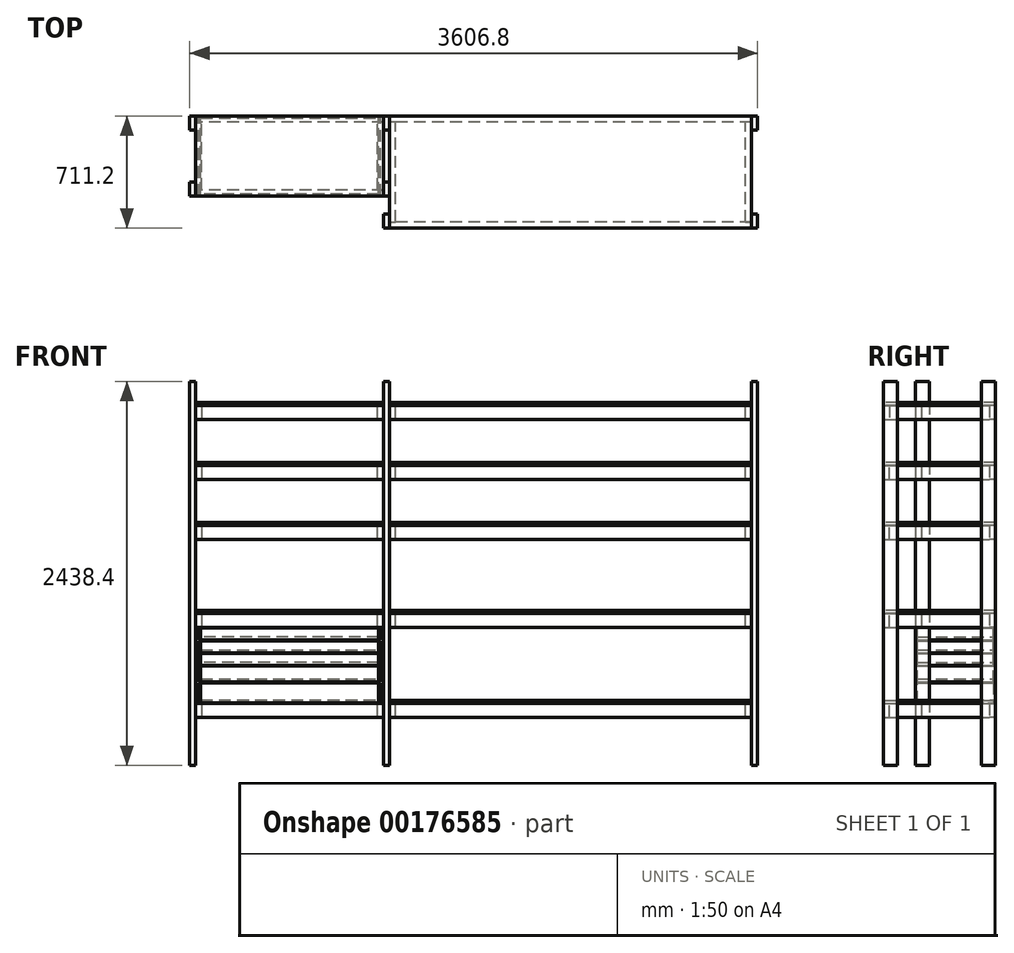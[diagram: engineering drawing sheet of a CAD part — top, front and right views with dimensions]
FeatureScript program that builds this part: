
annotation { "Feature Type Name" : "Feature", "Feature Type Description" : "" }
export const myFeature = defineFeature(function(context is Context, id is Id, definition is map)
    precondition{}
    {
        {
            var Q0;
            Q0=qCreatedBy(makeId("Top.planeOp"),FACE);
            var sketch = newSketch(context, id + "F0", { "sketchPlane" : qUnion([Q0])});
            skLineSegment(sketch, "E0.bottom", {"start": v(0, 0) * mm, "end": v(38.1, 0) * mm});
            skLineSegment(sketch, "E0.top", {"start": v(0, -88.9) * mm, "end": v(38.1, -88.9) * mm});
            skLineSegment(sketch, "E0.left", {"start": v(0, 0) * mm, "end": v(0, -88.9) * mm});
            skLineSegment(sketch, "E0.right", {"start": v(38.1, 0) * mm, "end": v(38.1, -88.9) * mm});
            skLineSegment(sketch, "E1.bottom", {"start": v(0, -508) * mm, "end": v(38.1, -508) * mm});
            skLineSegment(sketch, "E1.top", {"start": v(0, -419.1) * mm, "end": v(38.1, -419.1) * mm});
            skLineSegment(sketch, "E1.left", {"start": v(0, -508) * mm, "end": v(0, -419.1) * mm});
            skLineSegment(sketch, "E1.right", {"start": v(38.1, -508) * mm, "end": v(38.1, -419.1) * mm});
            skLineSegment(sketch, "E2.bottom", {"start": v(1270, 0) * mm, "end": v(1231.9, 0) * mm});
            skLineSegment(sketch, "E2.top", {"start": v(1270, -88.9) * mm, "end": v(1231.9, -88.9) * mm});
            skLineSegment(sketch, "E2.left", {"start": v(1270, 0) * mm, "end": v(1270, -88.9) * mm});
            skLineSegment(sketch, "E2.right", {"start": v(1231.9, 0) * mm, "end": v(1231.9, -88.9) * mm});
            skLineSegment(sketch, "E3.bottom", {"start": v(1270, -508) * mm, "end": v(1231.9, -508) * mm});
            skLineSegment(sketch, "E3.top", {"start": v(1270, -419.1) * mm, "end": v(1231.9, -419.1) * mm});
            skLineSegment(sketch, "E3.left", {"start": v(1270, -508) * mm, "end": v(1270, -419.1) * mm});
            skLineSegment(sketch, "E3.right", {"start": v(1231.9, -508) * mm, "end": v(1231.9, -419.1) * mm});
            skLineSegment(sketch, "E4.bottom", {"start": v(1231.9, -622.3) * mm, "end": v(1270, -622.3) * mm});
            skLineSegment(sketch, "E4.top", {"start": v(1231.9, -711.2) * mm, "end": v(1270, -711.2) * mm});
            skLineSegment(sketch, "E4.left", {"start": v(1231.9, -622.3) * mm, "end": v(1231.9, -711.2) * mm});
            skLineSegment(sketch, "E4.right", {"start": v(1270, -622.3) * mm, "end": v(1270, -711.2) * mm});
            skLineSegment(sketch, "E5.bottom", {"start": v(3606.8, 0) * mm, "end": v(3568.7, 0) * mm});
            skLineSegment(sketch, "E5.top", {"start": v(3606.8, -88.9) * mm, "end": v(3568.7, -88.9) * mm});
            skLineSegment(sketch, "E5.left", {"start": v(3606.8, 0) * mm, "end": v(3606.8, -88.9) * mm});
            skLineSegment(sketch, "E5.right", {"start": v(3568.7, 0) * mm, "end": v(3568.7, -88.9) * mm});
            skLineSegment(sketch, "E6.bottom", {"start": v(3606.8, -711.2) * mm, "end": v(3568.7, -711.2) * mm});
            skLineSegment(sketch, "E6.top", {"start": v(3606.8, -622.3) * mm, "end": v(3568.7, -622.3) * mm});
            skLineSegment(sketch, "E6.left", {"start": v(3606.8, -711.2) * mm, "end": v(3606.8, -622.3) * mm});
            skLineSegment(sketch, "E6.right", {"start": v(3568.7, -711.2) * mm, "end": v(3568.7, -622.3) * mm});
            skSolve(sketch);
        }
        {
            var Q0;
            Q0 = qSketchRegion(id + "F0", true);
            extrude(context, id + "F1", {"entities" : qUnion([Q0]), "depth" : 2438.4 * mm});
        }
        {
            var Q0;
            Q0=qCreatedBy(makeId("Front.planeOp"),FACE);
            var sketch = newSketch(context, id + "F2", { "sketchPlane" : qUnion([Q0])});
            skLineSegment(sketch, "E7.bottom", {"start": v(38.1, 304.8) * mm, "end": v(76.2, 304.8) * mm});
            skLineSegment(sketch, "E7.top", {"start": v(38.1, 393.7) * mm, "end": v(76.2, 393.7) * mm});
            skLineSegment(sketch, "E7.left", {"start": v(38.1, 304.8) * mm, "end": v(38.1, 393.7) * mm});
            skLineSegment(sketch, "E7.right", {"start": v(76.2, 304.8) * mm, "end": v(76.2, 393.7) * mm});
            skLineSegment(sketch, "E8.bottom", {"start": v(38.1, 876.3) * mm, "end": v(76.2, 876.3) * mm});
            skLineSegment(sketch, "E8.top", {"start": v(38.1, 965.2) * mm, "end": v(76.2, 965.2) * mm});
            skLineSegment(sketch, "E8.left", {"start": v(38.1, 876.3) * mm, "end": v(38.1, 965.2) * mm});
            skLineSegment(sketch, "E8.right", {"start": v(76.2, 876.3) * mm, "end": v(76.2, 965.2) * mm});
            skLineSegment(sketch, "E9.bottom", {"start": v(76.2, 1435.1) * mm, "end": v(38.1, 1435.1) * mm});
            skLineSegment(sketch, "E9.top", {"start": v(76.2, 1524) * mm, "end": v(38.1, 1524) * mm});
            skLineSegment(sketch, "E9.left", {"start": v(76.2, 1435.1) * mm, "end": v(76.2, 1524) * mm});
            skLineSegment(sketch, "E9.right", {"start": v(38.1, 1435.1) * mm, "end": v(38.1, 1524) * mm});
            skLineSegment(sketch, "E10.bottom", {"start": v(38.1, 1816.1) * mm, "end": v(76.2, 1816.1) * mm});
            skLineSegment(sketch, "E10.top", {"start": v(38.1, 1905) * mm, "end": v(76.2, 1905) * mm});
            skLineSegment(sketch, "E10.left", {"start": v(38.1, 1816.1) * mm, "end": v(38.1, 1905) * mm});
            skLineSegment(sketch, "E10.right", {"start": v(76.2, 1816.1) * mm, "end": v(76.2, 1905) * mm});
            skLineSegment(sketch, "E11.bottom", {"start": v(38.1, 2197.1) * mm, "end": v(76.2, 2197.1) * mm});
            skLineSegment(sketch, "E11.top", {"start": v(38.1, 2286) * mm, "end": v(76.2, 2286) * mm});
            skLineSegment(sketch, "E11.left", {"start": v(38.1, 2197.1) * mm, "end": v(38.1, 2286) * mm});
            skLineSegment(sketch, "E11.right", {"start": v(76.2, 2197.1) * mm, "end": v(76.2, 2286) * mm});
            skLineSegment(sketch, "E12", {"start": v(76.2, 774.7) * mm, "end": v(165.1, 774.7) * mm, "construction": true});
            skLineSegment(sketch, "E13", {"start": v(76.2, 698.5) * mm, "end": v(165.1, 698.5) * mm, "construction": true});
            skLineSegment(sketch, "E14", {"start": v(76.2, 622.3) * mm, "end": v(165.1, 622.3) * mm, "construction": true});
            skLineSegment(sketch, "E15", {"start": v(76.2, 520.7) * mm, "end": v(165.1, 520.7) * mm, "construction": true});
            skLineSegment(sketch, "E16", {"start": v(76.2, 393.7) * mm, "end": v(165.1, 393.7) * mm, "construction": true});
            skLineSegment(sketch, "E17.bottom", {"start": v(1231.9, 2286) * mm, "end": v(1193.8, 2286) * mm});
            skLineSegment(sketch, "E17.top", {"start": v(1231.9, 2197.1) * mm, "end": v(1193.8, 2197.1) * mm});
            skLineSegment(sketch, "E17.left", {"start": v(1231.9, 2286) * mm, "end": v(1231.9, 2197.1) * mm});
            skLineSegment(sketch, "E17.right", {"start": v(1193.8, 2286) * mm, "end": v(1193.8, 2197.1) * mm});
            skLineSegment(sketch, "E18.bottom", {"start": v(1231.9, 1905) * mm, "end": v(1193.8, 1905) * mm});
            skLineSegment(sketch, "E18.top", {"start": v(1231.9, 1816.1) * mm, "end": v(1193.8, 1816.1) * mm});
            skLineSegment(sketch, "E18.left", {"start": v(1231.9, 1905) * mm, "end": v(1231.9, 1816.1) * mm});
            skLineSegment(sketch, "E18.right", {"start": v(1193.8, 1905) * mm, "end": v(1193.8, 1816.1) * mm});
            skLineSegment(sketch, "E19.bottom", {"start": v(1231.9, 1524) * mm, "end": v(1193.8, 1524) * mm});
            skLineSegment(sketch, "E19.top", {"start": v(1231.9, 1435.1) * mm, "end": v(1193.8, 1435.1) * mm});
            skLineSegment(sketch, "E19.left", {"start": v(1231.9, 1524) * mm, "end": v(1231.9, 1435.1) * mm});
            skLineSegment(sketch, "E19.right", {"start": v(1193.8, 1524) * mm, "end": v(1193.8, 1435.1) * mm});
            skLineSegment(sketch, "E20.bottom", {"start": v(1231.9, 965.2) * mm, "end": v(1193.8, 965.2) * mm});
            skLineSegment(sketch, "E20.top", {"start": v(1231.9, 876.3) * mm, "end": v(1193.8, 876.3) * mm});
            skLineSegment(sketch, "E20.left", {"start": v(1231.9, 965.2) * mm, "end": v(1231.9, 876.3) * mm});
            skLineSegment(sketch, "E20.right", {"start": v(1193.8, 965.2) * mm, "end": v(1193.8, 876.3) * mm});
            skLineSegment(sketch, "E21.bottom", {"start": v(1231.9, 393.7) * mm, "end": v(1193.8, 393.7) * mm});
            skLineSegment(sketch, "E21.top", {"start": v(1231.9, 304.8) * mm, "end": v(1193.8, 304.8) * mm});
            skLineSegment(sketch, "E21.left", {"start": v(1231.9, 393.7) * mm, "end": v(1231.9, 304.8) * mm});
            skLineSegment(sketch, "E21.right", {"start": v(1193.8, 393.7) * mm, "end": v(1193.8, 304.8) * mm});
            skSolve(sketch);
        }
        {
            var Q0;
            Q0=makeQuery(id+"F1.opExtrude","SWEPT_FACE",FACE,{"disambiguationData":[OSD([sQuery(id+"F0.wireOp",EDGE,"E0.right")])]});
            var sketch = newSketch(context, id + "F3", { "sketchPlane" : qUnion([Q0])});
            skLineSegment(sketch, "E22.bottom", {"start": v(0, 2286) * mm, "end": v(-38.1, 2286) * mm});
            skLineSegment(sketch, "E22.top", {"start": v(0, 2197.1) * mm, "end": v(-38.1, 2197.1) * mm});
            skLineSegment(sketch, "E22.left", {"start": v(0, 2286) * mm, "end": v(0, 2197.1) * mm});
            skLineSegment(sketch, "E22.right", {"start": v(-38.1, 2286) * mm, "end": v(-38.1, 2197.1) * mm});
            skLineSegment(sketch, "E23.bottom", {"start": v(0, 1905) * mm, "end": v(-38.1, 1905) * mm});
            skLineSegment(sketch, "E23.top", {"start": v(0, 1816.1) * mm, "end": v(-38.1, 1816.1) * mm});
            skLineSegment(sketch, "E23.left", {"start": v(0, 1905) * mm, "end": v(0, 1816.1) * mm});
            skLineSegment(sketch, "E23.right", {"start": v(-38.1, 1905) * mm, "end": v(-38.1, 1816.1) * mm});
            skLineSegment(sketch, "E24.bottom", {"start": v(0, 1524) * mm, "end": v(-38.1, 1524) * mm});
            skLineSegment(sketch, "E24.top", {"start": v(0, 1435.1) * mm, "end": v(-38.1, 1435.1) * mm});
            skLineSegment(sketch, "E24.left", {"start": v(0, 1524) * mm, "end": v(0, 1435.1) * mm});
            skLineSegment(sketch, "E24.right", {"start": v(-38.1, 1524) * mm, "end": v(-38.1, 1435.1) * mm});
            skLineSegment(sketch, "E25.bottom", {"start": v(0, 965.2) * mm, "end": v(-38.1, 965.2) * mm});
            skLineSegment(sketch, "E25.top", {"start": v(0, 876.3) * mm, "end": v(-38.1, 876.3) * mm});
            skLineSegment(sketch, "E25.left", {"start": v(0, 965.2) * mm, "end": v(0, 876.3) * mm});
            skLineSegment(sketch, "E25.right", {"start": v(-38.1, 965.2) * mm, "end": v(-38.1, 876.3) * mm});
            skLineSegment(sketch, "E26.bottom", {"start": v(0, 393.7) * mm, "end": v(-38.1, 393.7) * mm});
            skLineSegment(sketch, "E26.top", {"start": v(0, 304.8) * mm, "end": v(-38.1, 304.8) * mm});
            skLineSegment(sketch, "E26.left", {"start": v(0, 393.7) * mm, "end": v(0, 304.8) * mm});
            skLineSegment(sketch, "E26.right", {"start": v(-38.1, 393.7) * mm, "end": v(-38.1, 304.8) * mm});
            skLineSegment(sketch, "E27.bottom", {"start": v(-508, 2286) * mm, "end": v(-469.9, 2286) * mm});
            skLineSegment(sketch, "E27.top", {"start": v(-508, 2197.1) * mm, "end": v(-469.9, 2197.1) * mm});
            skLineSegment(sketch, "E27.left", {"start": v(-508, 2286) * mm, "end": v(-508, 2197.1) * mm});
            skLineSegment(sketch, "E27.right", {"start": v(-469.9, 2286) * mm, "end": v(-469.9, 2197.1) * mm});
            skLineSegment(sketch, "E28.bottom", {"start": v(-508, 1905) * mm, "end": v(-469.9, 1905) * mm});
            skLineSegment(sketch, "E28.top", {"start": v(-508, 1816.1) * mm, "end": v(-469.9, 1816.1) * mm});
            skLineSegment(sketch, "E28.left", {"start": v(-508, 1905) * mm, "end": v(-508, 1816.1) * mm});
            skLineSegment(sketch, "E28.right", {"start": v(-469.9, 1905) * mm, "end": v(-469.9, 1816.1) * mm});
            skLineSegment(sketch, "E29.bottom", {"start": v(-508, 1524) * mm, "end": v(-469.9, 1524) * mm});
            skLineSegment(sketch, "E29.top", {"start": v(-508, 1435.1) * mm, "end": v(-469.9, 1435.1) * mm});
            skLineSegment(sketch, "E29.left", {"start": v(-508, 1524) * mm, "end": v(-508, 1435.1) * mm});
            skLineSegment(sketch, "E29.right", {"start": v(-469.9, 1524) * mm, "end": v(-469.9, 1435.1) * mm});
            skLineSegment(sketch, "E30.bottom", {"start": v(-508, 965.2) * mm, "end": v(-469.9, 965.2) * mm});
            skLineSegment(sketch, "E30.top", {"start": v(-508, 876.3) * mm, "end": v(-469.9, 876.3) * mm});
            skLineSegment(sketch, "E30.left", {"start": v(-508, 965.2) * mm, "end": v(-508, 876.3) * mm});
            skLineSegment(sketch, "E30.right", {"start": v(-469.9, 965.2) * mm, "end": v(-469.9, 876.3) * mm});
            skLineSegment(sketch, "E31.bottom", {"start": v(-508, 393.7) * mm, "end": v(-469.9, 393.7) * mm});
            skLineSegment(sketch, "E31.top", {"start": v(-508, 304.8) * mm, "end": v(-469.9, 304.8) * mm});
            skLineSegment(sketch, "E31.left", {"start": v(-508, 393.7) * mm, "end": v(-508, 304.8) * mm});
            skLineSegment(sketch, "E31.right", {"start": v(-469.9, 393.7) * mm, "end": v(-469.9, 304.8) * mm});
            skSolve(sketch);
        }
        {
            var Q0;
            Q0 = qSketchRegion(id + "F3", true);
            var Q1;
            Q1=makeQuery(id+"F1.opExtrude","SWEPT_FACE",FACE,{"disambiguationData":[OSD([sQuery(id+"F0.wireOp",EDGE,"E2.right")])]});
            extrude(context, id + "F4", {"entities" : qUnion([Q0]), "endBound" : BoundingType.UP_TO_SURFACE, "endBoundEntityFace" : qUnion([Q1]), "depth" : 25.4 * mm});
        }
        {
            var Q0;
            Q0=makeQuery(id+"F1.opExtrude","SWEPT_FACE",FACE,{"disambiguationData":[OSD([sQuery(id+"F0.wireOp",EDGE,"E2.left")])]});
            var sketch = newSketch(context, id + "F5", { "sketchPlane" : qUnion([Q0])});
            skLineSegment(sketch, "E32.0", {"start": v(0, 2286) * mm, "end": v(-38.1, 2286) * mm});
            skLineSegment(sketch, "E32.1", {"start": v(0, 2197.1) * mm, "end": v(-38.1, 2197.1) * mm});
            skLineSegment(sketch, "E32.2", {"start": v(0, 2286) * mm, "end": v(0, 2197.1) * mm});
            skLineSegment(sketch, "E32.3", {"start": v(-38.1, 2286) * mm, "end": v(-38.1, 2197.1) * mm});
            skLineSegment(sketch, "E32.4", {"start": v(0, 1905) * mm, "end": v(-38.1, 1905) * mm});
            skLineSegment(sketch, "E32.5", {"start": v(0, 1816.1) * mm, "end": v(-38.1, 1816.1) * mm});
            skLineSegment(sketch, "E32.6", {"start": v(0, 1905) * mm, "end": v(0, 1816.1) * mm});
            skLineSegment(sketch, "E32.7", {"start": v(-38.1, 1905) * mm, "end": v(-38.1, 1816.1) * mm});
            skLineSegment(sketch, "E32.8", {"start": v(0, 1524) * mm, "end": v(-38.1, 1524) * mm});
            skLineSegment(sketch, "E32.9", {"start": v(0, 1435.1) * mm, "end": v(-38.1, 1435.1) * mm});
            skLineSegment(sketch, "E32.10", {"start": v(0, 1524) * mm, "end": v(0, 1435.1) * mm});
            skLineSegment(sketch, "E32.11", {"start": v(-38.1, 1524) * mm, "end": v(-38.1, 1435.1) * mm});
            skLineSegment(sketch, "E32.12", {"start": v(0, 965.2) * mm, "end": v(-38.1, 965.2) * mm});
            skLineSegment(sketch, "E32.13", {"start": v(0, 876.3) * mm, "end": v(-38.1, 876.3) * mm});
            skLineSegment(sketch, "E32.14", {"start": v(0, 965.2) * mm, "end": v(0, 876.3) * mm});
            skLineSegment(sketch, "E32.15", {"start": v(-38.1, 965.2) * mm, "end": v(-38.1, 876.3) * mm});
            skLineSegment(sketch, "E32.16", {"start": v(0, 393.7) * mm, "end": v(-38.1, 393.7) * mm});
            skLineSegment(sketch, "E32.17", {"start": v(0, 304.8) * mm, "end": v(-38.1, 304.8) * mm});
            skLineSegment(sketch, "E32.18", {"start": v(0, 393.7) * mm, "end": v(0, 304.8) * mm});
            skLineSegment(sketch, "E32.19", {"start": v(-38.1, 393.7) * mm, "end": v(-38.1, 304.8) * mm});
            skLineSegment(sketch, "E33.bottom", {"start": v(-711.2, 2286) * mm, "end": v(-673.1, 2286) * mm});
            skLineSegment(sketch, "E33.top", {"start": v(-711.2, 2197.1) * mm, "end": v(-673.1, 2197.1) * mm});
            skLineSegment(sketch, "E33.left", {"start": v(-711.2, 2286) * mm, "end": v(-711.2, 2197.1) * mm});
            skLineSegment(sketch, "E33.right", {"start": v(-673.1, 2286) * mm, "end": v(-673.1, 2197.1) * mm});
            skLineSegment(sketch, "E34.bottom", {"start": v(-711.2, 1905) * mm, "end": v(-673.1, 1905) * mm});
            skLineSegment(sketch, "E34.top", {"start": v(-711.2, 1816.1) * mm, "end": v(-673.1, 1816.1) * mm});
            skLineSegment(sketch, "E34.left", {"start": v(-711.2, 1905) * mm, "end": v(-711.2, 1816.1) * mm});
            skLineSegment(sketch, "E34.right", {"start": v(-673.1, 1905) * mm, "end": v(-673.1, 1816.1) * mm});
            skLineSegment(sketch, "E35.bottom", {"start": v(-711.2, 1524) * mm, "end": v(-673.1, 1524) * mm});
            skLineSegment(sketch, "E35.top", {"start": v(-711.2, 1435.1) * mm, "end": v(-673.1, 1435.1) * mm});
            skLineSegment(sketch, "E35.left", {"start": v(-711.2, 1524) * mm, "end": v(-711.2, 1435.1) * mm});
            skLineSegment(sketch, "E35.right", {"start": v(-673.1, 1524) * mm, "end": v(-673.1, 1435.1) * mm});
            skLineSegment(sketch, "E36.bottom", {"start": v(-711.2, 965.2) * mm, "end": v(-673.1, 965.2) * mm});
            skLineSegment(sketch, "E36.top", {"start": v(-711.2, 876.3) * mm, "end": v(-673.1, 876.3) * mm});
            skLineSegment(sketch, "E36.left", {"start": v(-711.2, 965.2) * mm, "end": v(-711.2, 876.3) * mm});
            skLineSegment(sketch, "E36.right", {"start": v(-673.1, 965.2) * mm, "end": v(-673.1, 876.3) * mm});
            skLineSegment(sketch, "E37.bottom", {"start": v(-711.2, 393.7) * mm, "end": v(-673.1, 393.7) * mm});
            skLineSegment(sketch, "E37.top", {"start": v(-711.2, 304.8) * mm, "end": v(-673.1, 304.8) * mm});
            skLineSegment(sketch, "E37.left", {"start": v(-711.2, 393.7) * mm, "end": v(-711.2, 304.8) * mm});
            skLineSegment(sketch, "E37.right", {"start": v(-673.1, 393.7) * mm, "end": v(-673.1, 304.8) * mm});
            skSolve(sketch);
        }
        {
            var Q0;
            Q0 = qSketchRegion(id + "F5", true);
            var Q1;
            Q1=makeQuery(id+"F1.opExtrude","SWEPT_FACE",FACE,{"disambiguationData":[OSD([sQuery(id+"F0.wireOp",EDGE,"E5.right")])]});
            extrude(context, id + "F6", {"entities" : qUnion([Q0]), "endBound" : BoundingType.UP_TO_SURFACE, "endBoundEntityFace" : qUnion([Q1]), "depth" : 25.4 * mm});
        }
        {
            var Q0;
            Q0=makeQuery(id+"F4.opExtrude","SWEPT_FACE",FACE,{"disambiguationData":[OSD([sQuery(id+"F3.wireOp",EDGE,"E22.right")])]});
            var sketch = newSketch(context, id + "F7", { "sketchPlane" : qUnion([Q0])});
            skLineSegment(sketch, "E38.0", {"start": v(0, 0) * mm, "end": v(38.1, 0) * mm});
            skLineSegment(sketch, "E38.1", {"start": v(0, 0) * mm, "end": v(38.1, 0) * mm});
            skLineSegment(sketch, "E38.4", {"start": v(0, 0) * mm, "end": v(38.1, 0) * mm});
            skLineSegment(sketch, "E38.5", {"start": v(0, 0) * mm, "end": v(38.1, 0) * mm});
            skLineSegment(sketch, "E38.8", {"start": v(1270, 0) * mm, "end": v(1231.9, 0) * mm});
            skLineSegment(sketch, "E38.9", {"start": v(1270, 0) * mm, "end": v(1231.9, 0) * mm});
            skLineSegment(sketch, "E38.12", {"start": v(1270, 0) * mm, "end": v(1231.9, 0) * mm});
            skLineSegment(sketch, "E38.13", {"start": v(1270, 0) * mm, "end": v(1231.9, 0) * mm});
            skLineSegment(sketch, "E38.16", {"start": v(1231.9, 0) * mm, "end": v(1270, 0) * mm});
            skLineSegment(sketch, "E38.17", {"start": v(1231.9, 0) * mm, "end": v(1270, 0) * mm});
            skLineSegment(sketch, "E38.20", {"start": v(3606.8, 0) * mm, "end": v(3568.7, 0) * mm});
            skLineSegment(sketch, "E38.21", {"start": v(3606.8, 0) * mm, "end": v(3568.7, 0) * mm});
            skLineSegment(sketch, "E38.24", {"start": v(3606.8, 0) * mm, "end": v(3568.7, 0) * mm});
            skLineSegment(sketch, "E38.25", {"start": v(3606.8, 0) * mm, "end": v(3568.7, 0) * mm});
            skLineSegment(sketch, "E38.28", {"start": v(38.1, 304.8) * mm, "end": v(76.2, 304.8) * mm});
            skLineSegment(sketch, "E38.29", {"start": v(38.1, 393.7) * mm, "end": v(76.2, 393.7) * mm});
            skLineSegment(sketch, "E38.30", {"start": v(38.1, 304.8) * mm, "end": v(38.1, 393.7) * mm});
            skLineSegment(sketch, "E38.31", {"start": v(76.2, 304.8) * mm, "end": v(76.2, 393.7) * mm});
            skLineSegment(sketch, "E38.32", {"start": v(38.1, 876.3) * mm, "end": v(76.2, 876.3) * mm});
            skLineSegment(sketch, "E38.33", {"start": v(38.1, 965.2) * mm, "end": v(76.2, 965.2) * mm});
            skLineSegment(sketch, "E38.34", {"start": v(38.1, 876.3) * mm, "end": v(38.1, 965.2) * mm});
            skLineSegment(sketch, "E38.35", {"start": v(76.2, 876.3) * mm, "end": v(76.2, 965.2) * mm});
            skLineSegment(sketch, "E38.36", {"start": v(76.2, 1435.1) * mm, "end": v(38.1, 1435.1) * mm});
            skLineSegment(sketch, "E38.37", {"start": v(76.2, 1524) * mm, "end": v(38.1, 1524) * mm});
            skLineSegment(sketch, "E38.38", {"start": v(76.2, 1435.1) * mm, "end": v(76.2, 1524) * mm});
            skLineSegment(sketch, "E38.39", {"start": v(38.1, 1435.1) * mm, "end": v(38.1, 1524) * mm});
            skLineSegment(sketch, "E38.40", {"start": v(38.1, 1816.1) * mm, "end": v(76.2, 1816.1) * mm});
            skLineSegment(sketch, "E38.41", {"start": v(38.1, 1905) * mm, "end": v(76.2, 1905) * mm});
            skLineSegment(sketch, "E38.42", {"start": v(38.1, 1816.1) * mm, "end": v(38.1, 1905) * mm});
            skLineSegment(sketch, "E38.43", {"start": v(76.2, 1816.1) * mm, "end": v(76.2, 1905) * mm});
            skLineSegment(sketch, "E38.44", {"start": v(38.1, 2197.1) * mm, "end": v(76.2, 2197.1) * mm});
            skLineSegment(sketch, "E38.45", {"start": v(38.1, 2286) * mm, "end": v(76.2, 2286) * mm});
            skLineSegment(sketch, "E38.46", {"start": v(38.1, 2197.1) * mm, "end": v(38.1, 2286) * mm});
            skLineSegment(sketch, "E38.47", {"start": v(76.2, 2197.1) * mm, "end": v(76.2, 2286) * mm});
            skLineSegment(sketch, "E38.48", {"start": v(76.2, 774.7) * mm, "end": v(165.1, 774.7) * mm});
            skLineSegment(sketch, "E38.49", {"start": v(76.2, 698.5) * mm, "end": v(165.1, 698.5) * mm});
            skLineSegment(sketch, "E38.50", {"start": v(76.2, 622.3) * mm, "end": v(165.1, 622.3) * mm});
            skLineSegment(sketch, "E38.51", {"start": v(76.2, 520.7) * mm, "end": v(165.1, 520.7) * mm});
            skLineSegment(sketch, "E38.52", {"start": v(76.2, 393.7) * mm, "end": v(165.1, 393.7) * mm});
            skLineSegment(sketch, "E38.53", {"start": v(1231.9, 2286) * mm, "end": v(1193.8, 2286) * mm});
            skLineSegment(sketch, "E38.54", {"start": v(1231.9, 2197.1) * mm, "end": v(1193.8, 2197.1) * mm});
            skLineSegment(sketch, "E38.55", {"start": v(1231.9, 2286) * mm, "end": v(1231.9, 2197.1) * mm});
            skLineSegment(sketch, "E38.56", {"start": v(1193.8, 2286) * mm, "end": v(1193.8, 2197.1) * mm});
            skLineSegment(sketch, "E38.57", {"start": v(1231.9, 1905) * mm, "end": v(1193.8, 1905) * mm});
            skLineSegment(sketch, "E38.58", {"start": v(1231.9, 1816.1) * mm, "end": v(1193.8, 1816.1) * mm});
            skLineSegment(sketch, "E38.59", {"start": v(1231.9, 1905) * mm, "end": v(1231.9, 1816.1) * mm});
            skLineSegment(sketch, "E38.60", {"start": v(1193.8, 1905) * mm, "end": v(1193.8, 1816.1) * mm});
            skLineSegment(sketch, "E38.61", {"start": v(1231.9, 1524) * mm, "end": v(1193.8, 1524) * mm});
            skLineSegment(sketch, "E38.62", {"start": v(1231.9, 1435.1) * mm, "end": v(1193.8, 1435.1) * mm});
            skLineSegment(sketch, "E38.63", {"start": v(1231.9, 1524) * mm, "end": v(1231.9, 1435.1) * mm});
            skLineSegment(sketch, "E38.64", {"start": v(1193.8, 1524) * mm, "end": v(1193.8, 1435.1) * mm});
            skLineSegment(sketch, "E38.65", {"start": v(1231.9, 965.2) * mm, "end": v(1193.8, 965.2) * mm});
            skLineSegment(sketch, "E38.66", {"start": v(1231.9, 876.3) * mm, "end": v(1193.8, 876.3) * mm});
            skLineSegment(sketch, "E38.67", {"start": v(1231.9, 965.2) * mm, "end": v(1231.9, 876.3) * mm});
            skLineSegment(sketch, "E38.68", {"start": v(1193.8, 965.2) * mm, "end": v(1193.8, 876.3) * mm});
            skLineSegment(sketch, "E38.69", {"start": v(1231.9, 393.7) * mm, "end": v(1193.8, 393.7) * mm});
            skLineSegment(sketch, "E38.70", {"start": v(1231.9, 304.8) * mm, "end": v(1193.8, 304.8) * mm});
            skLineSegment(sketch, "E38.71", {"start": v(1231.9, 393.7) * mm, "end": v(1231.9, 304.8) * mm});
            skLineSegment(sketch, "E38.72", {"start": v(1193.8, 393.7) * mm, "end": v(1193.8, 304.8) * mm});
            skSolve(sketch);
        }
        {
            var Q0;
            Q0 = qSketchRegion(id + "F7", true);
            var Q1;
            Q1=makeQuery(id+"F4.opExtrude","SWEPT_FACE",FACE,{"disambiguationData":[OSD([sQuery(id+"F3.wireOp",EDGE,"E27.right")])]});
            extrude(context, id + "F8", {"entities" : qUnion([Q0]), "endBound" : BoundingType.UP_TO_SURFACE, "endBoundEntityFace" : qUnion([Q1]), "depth" : 25.4 * mm});
        }
        {
            var Q0;
            {var subQ0=sQuery(id+"F7.wireOp",EDGE,"E38.47");Q0=makeQuery(id+"F7.imprint","IMPRINT",FACE,{"disambiguationData":[TD([[makeQuery(id+"F7.imprint","IMPRINT",EDGE,{"derivedFrom":subQ0}),-1.0]])]});}
            var sketch = newSketch(context, id + "F9", { "sketchPlane" : qUnion([Q0])});
            skLineSegment(sketch, "E39.bottom", {"start": v(1308.1, 2286) * mm, "end": v(1270, 2286) * mm});
            skLineSegment(sketch, "E39.top", {"start": v(1308.1, 2197.1) * mm, "end": v(1270, 2197.1) * mm});
            skLineSegment(sketch, "E39.left", {"start": v(1308.1, 2286) * mm, "end": v(1308.1, 2197.1) * mm});
            skLineSegment(sketch, "E39.right", {"start": v(1270, 2286) * mm, "end": v(1270, 2197.1) * mm});
            skLineSegment(sketch, "E40.bottom", {"start": v(3568.7, 2286) * mm, "end": v(3530.6, 2286) * mm});
            skLineSegment(sketch, "E40.top", {"start": v(3568.7, 2197.1) * mm, "end": v(3530.6, 2197.1) * mm});
            skLineSegment(sketch, "E40.left", {"start": v(3568.7, 2286) * mm, "end": v(3568.7, 2197.1) * mm});
            skLineSegment(sketch, "E40.right", {"start": v(3530.6, 2286) * mm, "end": v(3530.6, 2197.1) * mm});
            skLineSegment(sketch, "E41.bottom", {"start": v(1308.1, 1905) * mm, "end": v(1270, 1905) * mm});
            skLineSegment(sketch, "E41.top", {"start": v(1308.1, 1816.1) * mm, "end": v(1270, 1816.1) * mm});
            skLineSegment(sketch, "E41.left", {"start": v(1308.1, 1905) * mm, "end": v(1308.1, 1816.1) * mm});
            skLineSegment(sketch, "E41.right", {"start": v(1270, 1905) * mm, "end": v(1270, 1816.1) * mm});
            skLineSegment(sketch, "E42.bottom", {"start": v(1308.1, 1524) * mm, "end": v(1270, 1524) * mm});
            skLineSegment(sketch, "E42.top", {"start": v(1308.1, 1435.1) * mm, "end": v(1270, 1435.1) * mm});
            skLineSegment(sketch, "E42.left", {"start": v(1308.1, 1524) * mm, "end": v(1308.1, 1435.1) * mm});
            skLineSegment(sketch, "E42.right", {"start": v(1270, 1524) * mm, "end": v(1270, 1435.1) * mm});
            skLineSegment(sketch, "E43.bottom", {"start": v(1308.1, 965.2) * mm, "end": v(1270, 965.2) * mm});
            skLineSegment(sketch, "E43.top", {"start": v(1308.1, 876.3) * mm, "end": v(1270, 876.3) * mm});
            skLineSegment(sketch, "E43.left", {"start": v(1308.1, 965.2) * mm, "end": v(1308.1, 876.3) * mm});
            skLineSegment(sketch, "E43.right", {"start": v(1270, 965.2) * mm, "end": v(1270, 876.3) * mm});
            skLineSegment(sketch, "E44.bottom", {"start": v(1308.1, 393.7) * mm, "end": v(1270, 393.7) * mm});
            skLineSegment(sketch, "E44.top", {"start": v(1308.1, 304.8) * mm, "end": v(1270, 304.8) * mm});
            skLineSegment(sketch, "E44.left", {"start": v(1308.1, 393.7) * mm, "end": v(1308.1, 304.8) * mm});
            skLineSegment(sketch, "E44.right", {"start": v(1270, 393.7) * mm, "end": v(1270, 304.8) * mm});
            skLineSegment(sketch, "E45.bottom", {"start": v(3568.7, 1905) * mm, "end": v(3530.6, 1905) * mm});
            skLineSegment(sketch, "E45.top", {"start": v(3568.7, 1816.1) * mm, "end": v(3530.6, 1816.1) * mm});
            skLineSegment(sketch, "E45.left", {"start": v(3568.7, 1905) * mm, "end": v(3568.7, 1816.1) * mm});
            skLineSegment(sketch, "E45.right", {"start": v(3530.6, 1905) * mm, "end": v(3530.6, 1816.1) * mm});
            skLineSegment(sketch, "E46.bottom", {"start": v(3568.7, 1524) * mm, "end": v(3530.6, 1524) * mm});
            skLineSegment(sketch, "E46.top", {"start": v(3568.7, 1435.1) * mm, "end": v(3530.6, 1435.1) * mm});
            skLineSegment(sketch, "E46.left", {"start": v(3568.7, 1524) * mm, "end": v(3568.7, 1435.1) * mm});
            skLineSegment(sketch, "E46.right", {"start": v(3530.6, 1524) * mm, "end": v(3530.6, 1435.1) * mm});
            skLineSegment(sketch, "E47.bottom", {"start": v(3568.7, 965.2) * mm, "end": v(3530.6, 965.2) * mm});
            skLineSegment(sketch, "E47.top", {"start": v(3568.7, 876.3) * mm, "end": v(3530.6, 876.3) * mm});
            skLineSegment(sketch, "E47.left", {"start": v(3568.7, 965.2) * mm, "end": v(3568.7, 876.3) * mm});
            skLineSegment(sketch, "E47.right", {"start": v(3530.6, 965.2) * mm, "end": v(3530.6, 876.3) * mm});
            skLineSegment(sketch, "E48.bottom", {"start": v(3568.7, 393.7) * mm, "end": v(3530.6, 393.7) * mm});
            skLineSegment(sketch, "E48.top", {"start": v(3568.7, 304.8) * mm, "end": v(3530.6, 304.8) * mm});
            skLineSegment(sketch, "E48.left", {"start": v(3568.7, 393.7) * mm, "end": v(3568.7, 304.8) * mm});
            skLineSegment(sketch, "E48.right", {"start": v(3530.6, 393.7) * mm, "end": v(3530.6, 304.8) * mm});
            skSolve(sketch);
        }
        {
            var Q0;
            Q0 = qSketchRegion(id + "F9", true);
            var Q1;
            Q1=makeQuery(id+"F6.opExtrude","SWEPT_FACE",FACE,{"disambiguationData":[OSD([sQuery(id+"F5.wireOp",EDGE,"E33.right")])]});
            extrude(context, id + "F10", {"entities" : qUnion([Q0]), "endBound" : BoundingType.UP_TO_SURFACE, "endBoundEntityFace" : qUnion([Q1]), "depth" : 25.4 * mm});
        }
        {
            var Q0;
            Q0=makeQuery(id+"F1.opExtrude","SWEPT_FACE",FACE,{"disambiguationData":[OSD([sQuery(id+"F0.wireOp",EDGE,"E1.right")])]});
            var sketch = newSketch(context, id + "F11", { "sketchPlane" : qUnion([Q0])});
            skLineSegment(sketch, "E49.bottom", {"start": v(-508, 1905) * mm, "end": v(0, 1905) * mm});
            skLineSegment(sketch, "E49.top", {"start": v(-508, 1924.05) * mm, "end": v(0, 1924.05) * mm});
            skLineSegment(sketch, "E49.left", {"start": v(-508, 1905) * mm, "end": v(-508, 1924.05) * mm});
            skLineSegment(sketch, "E49.right", {"start": v(0, 1905) * mm, "end": v(0, 1924.05) * mm});
            skLineSegment(sketch, "E50.bottom", {"start": v(-508, 2286) * mm, "end": v(0, 2286) * mm});
            skLineSegment(sketch, "E50.top", {"start": v(-508, 2305.05) * mm, "end": v(0, 2305.05) * mm});
            skLineSegment(sketch, "E50.left", {"start": v(-508, 2286) * mm, "end": v(-508, 2305.05) * mm});
            skLineSegment(sketch, "E50.right", {"start": v(0, 2286) * mm, "end": v(0, 2305.05) * mm});
            skLineSegment(sketch, "E51.bottom", {"start": v(-508, 1524) * mm, "end": v(0, 1524) * mm});
            skLineSegment(sketch, "E51.top", {"start": v(-508, 1543.05) * mm, "end": v(0, 1543.05) * mm});
            skLineSegment(sketch, "E51.left", {"start": v(-508, 1524) * mm, "end": v(-508, 1543.05) * mm});
            skLineSegment(sketch, "E51.right", {"start": v(0, 1524) * mm, "end": v(0, 1543.05) * mm});
            skLineSegment(sketch, "E52.bottom", {"start": v(-508, 965.2) * mm, "end": v(0, 965.2) * mm});
            skLineSegment(sketch, "E52.top", {"start": v(-508, 984.25) * mm, "end": v(0, 984.25) * mm});
            skLineSegment(sketch, "E52.left", {"start": v(-508, 965.2) * mm, "end": v(-508, 984.25) * mm});
            skLineSegment(sketch, "E52.right", {"start": v(0, 965.2) * mm, "end": v(0, 984.25) * mm});
            skSolve(sketch);
        }
        {
            var Q0;
            Q0 = qSketchRegion(id + "F11", true);
            var Q1;
            Q1=makeQuery(id+"F1.opExtrude","SWEPT_FACE",FACE,{"disambiguationData":[OSD([sQuery(id+"F0.wireOp",EDGE,"E3.right")])]});
            extrude(context, id + "F12", {"entities" : qUnion([Q0]), "endBound" : BoundingType.UP_TO_SURFACE, "endBoundEntityFace" : qUnion([Q1]), "depth" : 25.4 * mm});
        }
        {
            var Q0;
            Q0=makeQuery(id+"F1.opExtrude","SWEPT_FACE",FACE,{"disambiguationData":[OSD([sQuery(id+"F0.wireOp",EDGE,"E2.left")])]});
            var sketch = newSketch(context, id + "F13", { "sketchPlane" : qUnion([Q0])});
            skLineSegment(sketch, "E53.0", {"start": v(-711.2, 1905) * mm, "end": v(0, 1905) * mm});
            skLineSegment(sketch, "E53.1", {"start": v(-711.2, 1924.05) * mm, "end": v(0, 1924.05) * mm});
            skLineSegment(sketch, "E53.2", {"start": v(-711.2, 1905) * mm, "end": v(-711.2, 1924.05) * mm});
            skLineSegment(sketch, "E53.3", {"start": v(0, 1905) * mm, "end": v(0, 1924.05) * mm});
            skLineSegment(sketch, "E53.4", {"start": v(-711.2, 2286) * mm, "end": v(0, 2286) * mm});
            skLineSegment(sketch, "E53.5", {"start": v(-711.2, 2305.05) * mm, "end": v(0, 2305.05) * mm});
            skLineSegment(sketch, "E53.6", {"start": v(-711.2, 2286) * mm, "end": v(-711.2, 2305.05) * mm});
            skLineSegment(sketch, "E53.7", {"start": v(0, 2286) * mm, "end": v(0, 2305.05) * mm});
            skLineSegment(sketch, "E53.8", {"start": v(-711.2, 1524) * mm, "end": v(0, 1524) * mm});
            skLineSegment(sketch, "E53.9", {"start": v(-711.2, 1543.05) * mm, "end": v(0, 1543.05) * mm});
            skLineSegment(sketch, "E53.10", {"start": v(-711.2, 1524) * mm, "end": v(-711.2, 1543.05) * mm});
            skLineSegment(sketch, "E53.11", {"start": v(0, 1524) * mm, "end": v(0, 1543.05) * mm});
            skLineSegment(sketch, "E53.12", {"start": v(-711.2, 965.2) * mm, "end": v(0, 965.2) * mm});
            skLineSegment(sketch, "E53.13", {"start": v(-711.2, 984.25) * mm, "end": v(0, 984.25) * mm});
            skLineSegment(sketch, "E53.15", {"start": v(0, 965.2) * mm, "end": v(0, 984.25) * mm});
            skLineSegment(sketch, "E54.bottom", {"start": v(0, 393.7) * mm, "end": v(-711.2, 393.7) * mm});
            skLineSegment(sketch, "E54.top", {"start": v(0, 412.75) * mm, "end": v(-711.2, 412.75) * mm});
            skLineSegment(sketch, "E54.left", {"start": v(0, 393.7) * mm, "end": v(0, 412.75) * mm});
            skLineSegment(sketch, "E54.right", {"start": v(-711.2, 393.7) * mm, "end": v(-711.2, 412.75) * mm});
            skLineSegment(sketch, "E55", {"start": v(-711.2, 984.25) * mm, "end": v(-711.2, 965.2) * mm});
            skSolve(sketch);
        }
        {
            var Q0;
            Q0 = qSketchRegion(id + "F13", true);
            var Q1;
            Q1=makeQuery(id+"F1.opExtrude","SWEPT_FACE",FACE,{"disambiguationData":[OSD([sQuery(id+"F0.wireOp",EDGE,"E6.right")])]});
            extrude(context, id + "F14", {"entities" : qUnion([Q0]), "endBound" : BoundingType.UP_TO_SURFACE, "endBoundEntityFace" : qUnion([Q1]), "depth" : 25.4 * mm});
        }
        {
            var Q0;
            Q0=qCreatedBy(makeId("Front.planeOp"),FACE);
            var sketch = newSketch(context, id + "F15", { "sketchPlane" : qUnion([Q0])});
            skLineSegment(sketch, "E56.bottom", {"start": v(57.15, 397.93) * mm, "end": v(69.85, 397.93) * mm});
            skLineSegment(sketch, "E56.top", {"start": v(57.15, 524.93) * mm, "end": v(69.85, 524.93) * mm});
            skLineSegment(sketch, "E56.left", {"start": v(57.15, 397.93) * mm, "end": v(57.15, 524.93) * mm});
            skLineSegment(sketch, "E56.right", {"start": v(69.85, 397.93) * mm, "end": v(69.85, 524.93) * mm});
            skLineSegment(sketch, "E57.bottom", {"start": v(57.15, 529.17) * mm, "end": v(69.85, 529.17) * mm});
            skLineSegment(sketch, "E57.top", {"start": v(57.15, 630.77) * mm, "end": v(69.85, 630.77) * mm});
            skLineSegment(sketch, "E57.left", {"start": v(57.15, 529.17) * mm, "end": v(57.15, 630.77) * mm});
            skLineSegment(sketch, "E57.right", {"start": v(69.85, 529.17) * mm, "end": v(69.85, 630.77) * mm});
            skLineSegment(sketch, "E58.bottom", {"start": v(57.15, 635) * mm, "end": v(69.85, 635) * mm});
            skLineSegment(sketch, "E58.top", {"start": v(57.15, 711.2) * mm, "end": v(69.85, 711.2) * mm});
            skLineSegment(sketch, "E58.left", {"start": v(57.15, 635) * mm, "end": v(57.15, 711.2) * mm});
            skLineSegment(sketch, "E58.right", {"start": v(69.85, 635) * mm, "end": v(69.85, 711.2) * mm});
            skLineSegment(sketch, "E59.bottom", {"start": v(57.15, 715.43) * mm, "end": v(69.85, 715.43) * mm});
            skLineSegment(sketch, "E59.top", {"start": v(57.15, 791.63) * mm, "end": v(69.85, 791.63) * mm});
            skLineSegment(sketch, "E59.left", {"start": v(57.15, 715.43) * mm, "end": v(57.15, 791.63) * mm});
            skLineSegment(sketch, "E59.right", {"start": v(69.85, 715.43) * mm, "end": v(69.85, 791.63) * mm});
            skLineSegment(sketch, "E60.bottom", {"start": v(57.15, 795.87) * mm, "end": v(69.85, 795.87) * mm});
            skLineSegment(sketch, "E60.top", {"start": v(57.15, 872.07) * mm, "end": v(69.85, 872.07) * mm});
            skLineSegment(sketch, "E60.left", {"start": v(57.15, 795.87) * mm, "end": v(57.15, 872.07) * mm});
            skLineSegment(sketch, "E60.right", {"start": v(69.85, 795.87) * mm, "end": v(69.85, 872.07) * mm});
            skLineSegment(sketch, "E61", {"start": v(57.15, 397.93) * mm, "end": v(57.15, 393.7) * mm, "construction": true});
            skLineSegment(sketch, "E62", {"start": v(57.15, 524.93) * mm, "end": v(57.15, 529.17) * mm, "construction": true});
            skLineSegment(sketch, "E63", {"start": v(57.15, 630.77) * mm, "end": v(57.15, 635) * mm, "construction": true});
            skLineSegment(sketch, "E64", {"start": v(57.15, 711.2) * mm, "end": v(57.15, 715.43) * mm, "construction": true});
            skLineSegment(sketch, "E65", {"start": v(57.15, 791.63) * mm, "end": v(57.15, 795.87) * mm, "construction": true});
            skLineSegment(sketch, "E66", {"start": v(57.15, 872.07) * mm, "end": v(57.15, 876.3) * mm, "construction": true});
            skLineSegment(sketch, "E67.bottom", {"start": v(1200.15, 872.07) * mm, "end": v(1212.85, 872.07) * mm});
            skLineSegment(sketch, "E67.top", {"start": v(1200.15, 795.87) * mm, "end": v(1212.85, 795.87) * mm});
            skLineSegment(sketch, "E67.left", {"start": v(1200.15, 872.07) * mm, "end": v(1200.15, 795.87) * mm});
            skLineSegment(sketch, "E67.right", {"start": v(1212.85, 872.07) * mm, "end": v(1212.85, 795.87) * mm});
            skLineSegment(sketch, "E68.bottom", {"start": v(1200.15, 791.63) * mm, "end": v(1212.85, 791.63) * mm});
            skLineSegment(sketch, "E68.top", {"start": v(1200.15, 715.43) * mm, "end": v(1212.85, 715.43) * mm});
            skLineSegment(sketch, "E68.left", {"start": v(1200.15, 791.63) * mm, "end": v(1200.15, 715.43) * mm});
            skLineSegment(sketch, "E68.right", {"start": v(1212.85, 791.63) * mm, "end": v(1212.85, 715.43) * mm});
            skLineSegment(sketch, "E69.bottom", {"start": v(1212.85, 711.2) * mm, "end": v(1200.15, 711.2) * mm});
            skLineSegment(sketch, "E69.top", {"start": v(1212.85, 635) * mm, "end": v(1200.15, 635) * mm});
            skLineSegment(sketch, "E69.left", {"start": v(1212.85, 711.2) * mm, "end": v(1212.85, 635) * mm});
            skLineSegment(sketch, "E69.right", {"start": v(1200.15, 711.2) * mm, "end": v(1200.15, 635) * mm});
            skLineSegment(sketch, "E70.bottom", {"start": v(1212.85, 630.77) * mm, "end": v(1200.15, 630.77) * mm});
            skLineSegment(sketch, "E70.top", {"start": v(1212.85, 529.17) * mm, "end": v(1200.15, 529.17) * mm});
            skLineSegment(sketch, "E70.left", {"start": v(1212.85, 630.77) * mm, "end": v(1212.85, 529.17) * mm});
            skLineSegment(sketch, "E70.right", {"start": v(1200.15, 630.77) * mm, "end": v(1200.15, 529.17) * mm});
            skLineSegment(sketch, "E71.bottom", {"start": v(1212.85, 524.93) * mm, "end": v(1200.15, 524.93) * mm});
            skLineSegment(sketch, "E71.top", {"start": v(1212.85, 397.93) * mm, "end": v(1200.15, 397.93) * mm});
            skLineSegment(sketch, "E71.left", {"start": v(1212.85, 524.93) * mm, "end": v(1212.85, 397.93) * mm});
            skLineSegment(sketch, "E71.right", {"start": v(1200.15, 524.93) * mm, "end": v(1200.15, 397.93) * mm});
            skSolve(sketch);
        }
        {
            var Q0;
            Q0 = qSketchRegion(id + "F15", true);
            var Q1;
            Q1=makeQuery(id+"F1.opExtrude","SWEPT_FACE",FACE,{"disambiguationData":[OSD([sQuery(id+"F0.wireOp",EDGE,"E1.bottom")])]});
            extrude(context, id + "F16", {"entities" : qUnion([Q0]), "endBound" : BoundingType.UP_TO_SURFACE, "endBoundEntityFace" : qUnion([Q1]), "depth" : 25.4 * mm});
        }
        {
            var Q0;
            Q0=makeQuery(id+"F16.opExtrude","SWEPT_FACE",FACE,{"disambiguationData":[OSD([sQuery(id+"F15.wireOp",EDGE,"E56.right")])]});
            var sketch = newSketch(context, id + "F17", { "sketchPlane" : qUnion([Q0])});
            skLineSegment(sketch, "E72.bottom", {"start": v(0, 524.93) * mm, "end": v(-12.7, 524.93) * mm});
            skLineSegment(sketch, "E72.top", {"start": v(0, 397.93) * mm, "end": v(-12.7, 397.93) * mm});
            skLineSegment(sketch, "E72.left", {"start": v(0, 524.93) * mm, "end": v(0, 397.93) * mm});
            skLineSegment(sketch, "E72.right", {"start": v(-12.7, 524.93) * mm, "end": v(-12.7, 397.93) * mm});
            skLineSegment(sketch, "E73.bottom", {"start": v(0, 529.17) * mm, "end": v(-12.7, 529.17) * mm});
            skLineSegment(sketch, "E73.top", {"start": v(0, 630.77) * mm, "end": v(-12.7, 630.77) * mm});
            skLineSegment(sketch, "E73.left", {"start": v(0, 529.17) * mm, "end": v(0, 630.77) * mm});
            skLineSegment(sketch, "E73.right", {"start": v(-12.7, 529.17) * mm, "end": v(-12.7, 630.77) * mm});
            skPoint(sketch, "E74.oppositeSnap0", {"position": v(-12.7, 579.97) * mm});
            skLineSegment(sketch, "E74.bottom", {"start": v(0, 635) * mm, "end": v(-12.7, 635) * mm});
            skLineSegment(sketch, "E74.top", {"start": v(0, 711.2) * mm, "end": v(-12.7, 711.2) * mm});
            skLineSegment(sketch, "E74.left", {"start": v(0, 635) * mm, "end": v(0, 711.2) * mm});
            skLineSegment(sketch, "E74.right", {"start": v(-12.7, 635) * mm, "end": v(-12.7, 711.2) * mm});
            skLineSegment(sketch, "E75.bottom", {"start": v(0, 715.43) * mm, "end": v(-12.7, 715.43) * mm});
            skLineSegment(sketch, "E75.top", {"start": v(0, 791.63) * mm, "end": v(-12.7, 791.63) * mm});
            skLineSegment(sketch, "E75.left", {"start": v(0, 715.43) * mm, "end": v(0, 791.63) * mm});
            skLineSegment(sketch, "E75.right", {"start": v(-12.7, 715.43) * mm, "end": v(-12.7, 791.63) * mm});
            skLineSegment(sketch, "E76.bottom", {"start": v(0, 795.87) * mm, "end": v(-12.7, 795.87) * mm});
            skLineSegment(sketch, "E76.top", {"start": v(0, 872.07) * mm, "end": v(-12.7, 872.07) * mm});
            skLineSegment(sketch, "E76.left", {"start": v(0, 795.87) * mm, "end": v(0, 872.07) * mm});
            skLineSegment(sketch, "E76.right", {"start": v(-12.7, 795.87) * mm, "end": v(-12.7, 872.07) * mm});
            skLineSegment(sketch, "E77.bottom", {"start": v(-495.3, 397.93) * mm, "end": v(-508, 397.93) * mm});
            skLineSegment(sketch, "E77.top", {"start": v(-495.3, 524.93) * mm, "end": v(-508, 524.93) * mm});
            skLineSegment(sketch, "E77.left", {"start": v(-495.3, 397.93) * mm, "end": v(-495.3, 524.93) * mm});
            skLineSegment(sketch, "E77.right", {"start": v(-508, 397.93) * mm, "end": v(-508, 524.93) * mm});
            skLineSegment(sketch, "E78.bottom", {"start": v(-508, 529.17) * mm, "end": v(-495.3, 529.17) * mm});
            skLineSegment(sketch, "E78.top", {"start": v(-508, 630.77) * mm, "end": v(-495.3, 630.77) * mm});
            skLineSegment(sketch, "E78.left", {"start": v(-508, 529.17) * mm, "end": v(-508, 630.77) * mm});
            skLineSegment(sketch, "E78.right", {"start": v(-495.3, 529.17) * mm, "end": v(-495.3, 630.77) * mm});
            skLineSegment(sketch, "E79.bottom", {"start": v(-508, 635) * mm, "end": v(-495.3, 635) * mm});
            skLineSegment(sketch, "E79.top", {"start": v(-508, 711.2) * mm, "end": v(-495.3, 711.2) * mm});
            skLineSegment(sketch, "E79.left", {"start": v(-508, 635) * mm, "end": v(-508, 711.2) * mm});
            skLineSegment(sketch, "E79.right", {"start": v(-495.3, 635) * mm, "end": v(-495.3, 711.2) * mm});
            skLineSegment(sketch, "E80.bottom", {"start": v(-508, 715.43) * mm, "end": v(-495.3, 715.43) * mm});
            skLineSegment(sketch, "E80.top", {"start": v(-508, 791.63) * mm, "end": v(-495.3, 791.63) * mm});
            skLineSegment(sketch, "E80.left", {"start": v(-508, 715.43) * mm, "end": v(-508, 791.63) * mm});
            skLineSegment(sketch, "E80.right", {"start": v(-495.3, 715.43) * mm, "end": v(-495.3, 791.63) * mm});
            skLineSegment(sketch, "E81.bottom", {"start": v(-508, 795.87) * mm, "end": v(-495.3, 795.87) * mm});
            skLineSegment(sketch, "E81.top", {"start": v(-508, 872.07) * mm, "end": v(-495.3, 872.07) * mm});
            skLineSegment(sketch, "E81.left", {"start": v(-508, 795.87) * mm, "end": v(-508, 872.07) * mm});
            skLineSegment(sketch, "E81.right", {"start": v(-495.3, 795.87) * mm, "end": v(-495.3, 872.07) * mm});
            skSolve(sketch);
        }
        {
            var Q0;
            Q0 = qSketchRegion(id + "F17", true);
            var Q1;
            Q1=makeQuery(id+"F16.opExtrude","SWEPT_FACE",FACE,{"disambiguationData":[OSD([sQuery(id+"F15.wireOp",EDGE,"E71.right")])]});
            extrude(context, id + "F18", {"entities" : qUnion([Q0]), "endBound" : BoundingType.UP_TO_SURFACE, "endBoundEntityFace" : qUnion([Q1]), "depth" : 25.4 * mm});
        }
        {
            var Q0;
            Q0=makeQuery(id+"F18.opExtrude","SWEPT_FACE",FACE,{"disambiguationData":[OSD([sQuery(id+"F17.wireOp",EDGE,"E72.right")])]});
            var sketch = newSketch(context, id + "F19", { "sketchPlane" : qUnion([Q0])});
            skLineSegment(sketch, "E82.bottom", {"start": v(69.85, 397.93) * mm, "end": v(1200.15, 397.93) * mm});
            skLineSegment(sketch, "E82.top", {"start": v(69.85, 416.98) * mm, "end": v(1200.15, 416.98) * mm});
            skLineSegment(sketch, "E82.left", {"start": v(69.85, 397.93) * mm, "end": v(69.85, 416.98) * mm});
            skLineSegment(sketch, "E82.right", {"start": v(1200.15, 397.93) * mm, "end": v(1200.15, 416.98) * mm});
            skLineSegment(sketch, "E83.bottom", {"start": v(69.85, 529.17) * mm, "end": v(1200.15, 529.17) * mm});
            skLineSegment(sketch, "E83.top", {"start": v(69.85, 548.22) * mm, "end": v(1200.15, 548.22) * mm});
            skLineSegment(sketch, "E83.left", {"start": v(69.85, 529.17) * mm, "end": v(69.85, 548.22) * mm});
            skLineSegment(sketch, "E83.right", {"start": v(1200.15, 529.17) * mm, "end": v(1200.15, 548.22) * mm});
            skLineSegment(sketch, "E84.bottom", {"start": v(1200.15, 635) * mm, "end": v(69.85, 635) * mm});
            skLineSegment(sketch, "E84.top", {"start": v(1200.15, 654.05) * mm, "end": v(69.85, 654.05) * mm});
            skLineSegment(sketch, "E84.left", {"start": v(1200.15, 635) * mm, "end": v(1200.15, 654.05) * mm});
            skLineSegment(sketch, "E84.right", {"start": v(69.85, 635) * mm, "end": v(69.85, 654.05) * mm});
            skLineSegment(sketch, "E85.bottom", {"start": v(69.85, 715.43) * mm, "end": v(1200.15, 715.43) * mm});
            skLineSegment(sketch, "E85.top", {"start": v(69.85, 734.48) * mm, "end": v(1200.15, 734.48) * mm});
            skLineSegment(sketch, "E85.left", {"start": v(69.85, 715.43) * mm, "end": v(69.85, 734.48) * mm});
            skLineSegment(sketch, "E85.right", {"start": v(1200.15, 715.43) * mm, "end": v(1200.15, 734.48) * mm});
            skLineSegment(sketch, "E86.bottom", {"start": v(1200.15, 795.87) * mm, "end": v(69.85, 795.87) * mm});
            skLineSegment(sketch, "E86.top", {"start": v(1200.15, 814.92) * mm, "end": v(69.85, 814.92) * mm});
            skLineSegment(sketch, "E86.left", {"start": v(1200.15, 795.87) * mm, "end": v(1200.15, 814.92) * mm});
            skLineSegment(sketch, "E86.right", {"start": v(69.85, 795.87) * mm, "end": v(69.85, 814.92) * mm});
            skSolve(sketch);
        }
        {
            var Q0;
            Q0 = qSketchRegion(id + "F19", true);
            var Q1;
            Q1=makeQuery(id+"F18.opExtrude","SWEPT_FACE",FACE,{"disambiguationData":[OSD([sQuery(id+"F17.wireOp",EDGE,"E77.left")])]});
            extrude(context, id + "F20", {"entities" : qUnion([Q0]), "endBound" : BoundingType.UP_TO_SURFACE, "endBoundEntityFace" : qUnion([Q1]), "depth" : 25.4 * mm});
        }
    });
